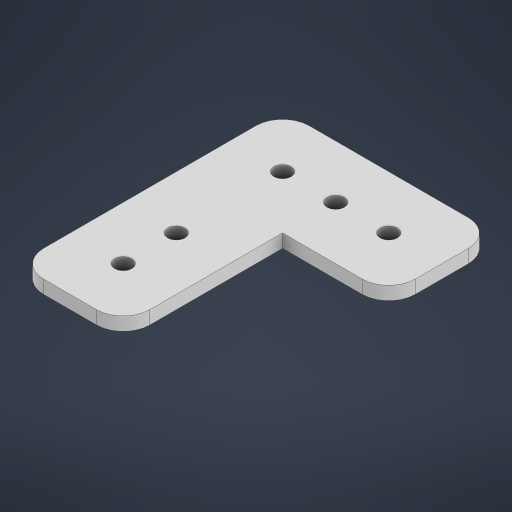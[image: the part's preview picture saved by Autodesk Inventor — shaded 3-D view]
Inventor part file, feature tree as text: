
AUTODESK INVENTOR PART (.ipt)
format: ipt  version: 2023 (Build 270158000, 158)  size: 194,048 bytes
history: native  units: in
note: dims shown in document units (in); Inventor stores cm internally (conversion verified against a paired STEP export)
features: extrude x1, fillet x1, sketch x1
ambient origin geometry x8: Origin, YZ Plane, XZ Plane, XY Plane, X Axis, Y Axis, Z Axis, Center Point
bodies: Solid1 (feature_tree)
feature tree (3):
  extrude  "Extrusion1"  Depth=2.5in
  fillet  "Fillet1"  Radius=1.0in
  sketch  "Sketch1"  dims[d22=2.0in d23=2.5in d24=1.0in d25=1.0in d26=0.1625in d27=0.1625in d28=0.5in d29=0.1625in d30=0.5in d31=0.1625in d32=1.0in d33=0.1625in d34=0.5in d35=0.125in d36=0.0in d37=0.25in]
